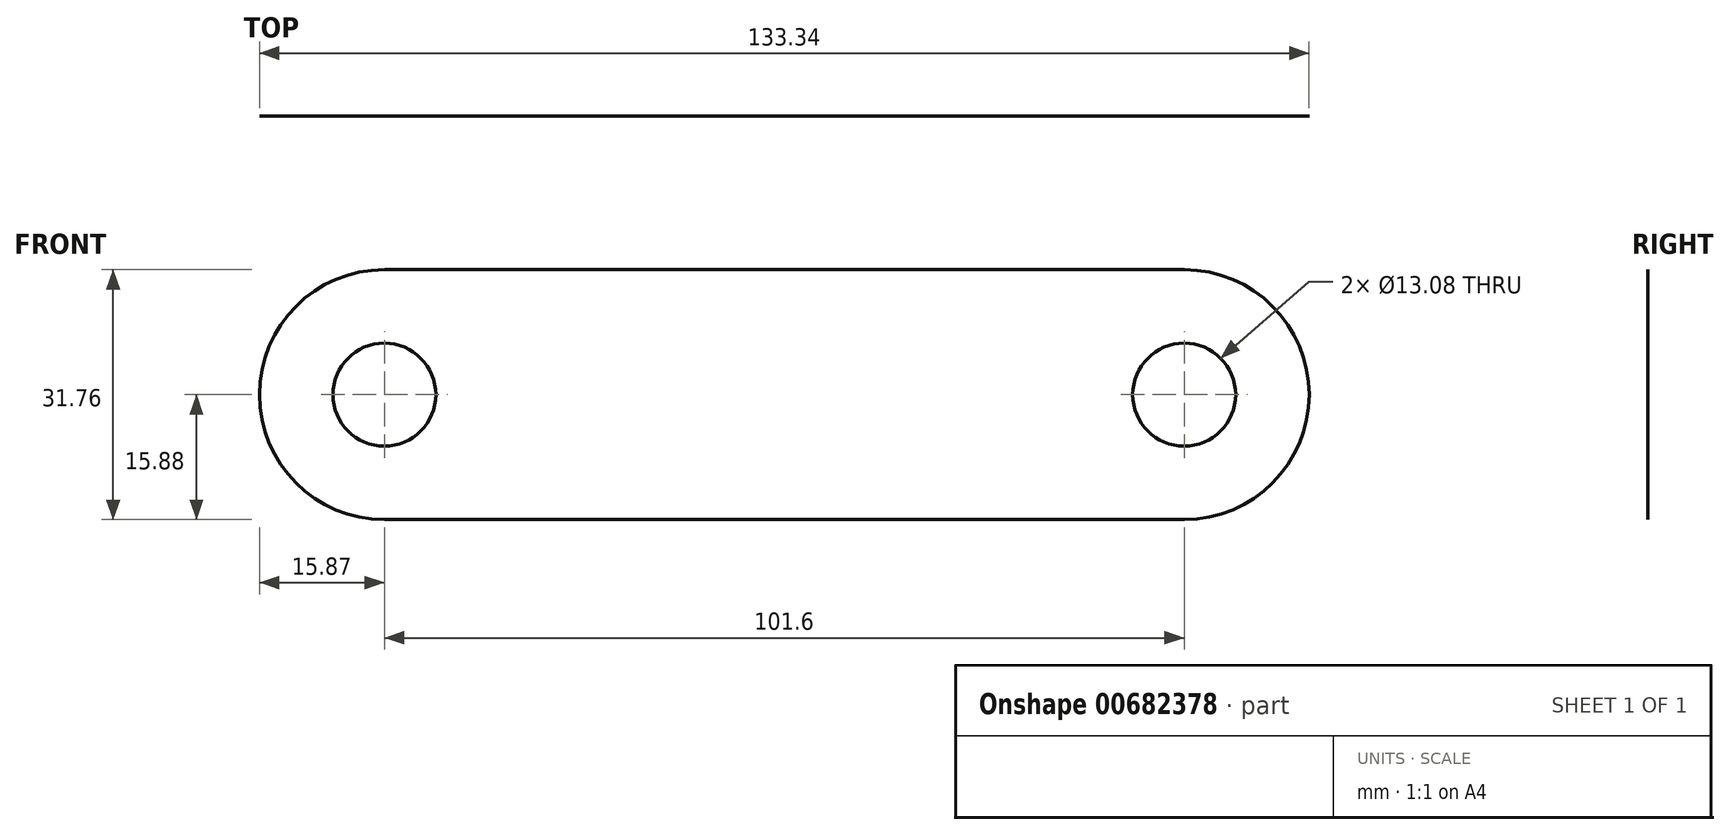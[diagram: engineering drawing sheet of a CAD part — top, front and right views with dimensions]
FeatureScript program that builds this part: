
annotation { "Feature Type Name" : "Feature", "Feature Type Description" : "" }
export const myFeature = defineFeature(function(context is Context, id is Id, definition is map)
    precondition{}
    {
        {
            var Q0;
            Q0=qCreatedBy(makeId("Front.planeOp"),FACE);
            var sketch = newSketch(context, id + "F0", { "sketchPlane" : qUnion([Q0])});
            skCircle(sketch, "E0", {"center": v(-50.8, 0) * mm, "radius": 6.54 * mm});
            skLineSegment(sketch, "E1", {"start": v(-50.8, 0) * mm, "end": v(0, 0) * mm, "construction": true});
            skCircle(sketch, "E2.MirrorC", {"center": v(50.8, 0) * mm, "radius": 6.54 * mm});
            skLineSegment(sketch, "E3.MirrorCS", {"start": v(50.8, 0) * mm, "end": v(0, 0) * mm, "construction": true});
            skArc(sketch, "E4", {"start": v(-50.8, 15.88) * mm, "mid": v(-66.68, 0) * mm, "end": v(-50.8, -15.88) * mm});
            skLineSegment(sketch, "E5", {"start": v(-50.8, 15.88) * mm, "end": v(0, 15.88) * mm});
            skLineSegment(sketch, "E6.MirrorCS", {"start": v(-50.8, -15.88) * mm, "end": v(0, -15.88) * mm});
            skLineSegment(sketch, "E7.MirrorCS", {"start": v(50.8, 15.88) * mm, "end": v(0, 15.88) * mm});
            skLineSegment(sketch, "E8.MirrorCS", {"start": v(50.8, -15.88) * mm, "end": v(0, -15.88) * mm});
            skArc(sketch, "E9.MirrorC", {"start": v(50.8, 15.88) * mm, "mid": v(66.68, 0) * mm, "end": v(50.8, -15.88) * mm});
            skSolve(sketch);
        }
        {
            var Q0;
            Q0=makeQuery(id+"F0.imprint","IMPRINT",FACE,{"disambiguationData":[TD([[makeQuery(id+"F0.imprint","IMPRINT",EDGE,{"derivedFrom":sQuery(id+"F0.wireOp",EDGE,"E0")}),-1.0]])]});
            extrude(context, id + "F1", {"entities" : qUnion([Q0]), "endBound" : BoundingType.SYMMETRIC, "depth" : 1 / 203.2 * mm, "offsetDistance" : 25.4 * mm});
        }
    });
